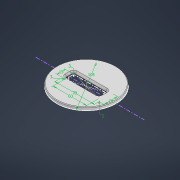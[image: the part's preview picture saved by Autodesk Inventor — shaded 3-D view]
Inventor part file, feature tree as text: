
AUTODESK INVENTOR PART (.ipt)
format: ipt  version: 2022 (Build 260153070, 153G)  size: 154,624 bytes
history: native  units: mm
features: other x3, extrude x2, chamfer x2, sketch x1
ambient origin geometry x8: Origin, YZ Plane, XZ Plane, XY Plane, X Axis, Y Axis, Z Axis, Center Point
bodies: Body1 (feature_tree)
feature tree (8):
  other  "Твердое тело1"
  sketch  "Эскиз1"
  extrude  "Выдавливание1"  Depth=105.0mm
  chamfer  "Фаска1"  Distance=60.0mm
  chamfer  "Фаска2"  Distance=15.0mm
  extrude  "Выдавливание2"  Depth=3.0mm
  other  "РабПлоскость1"
  other  "РабОсь3"
